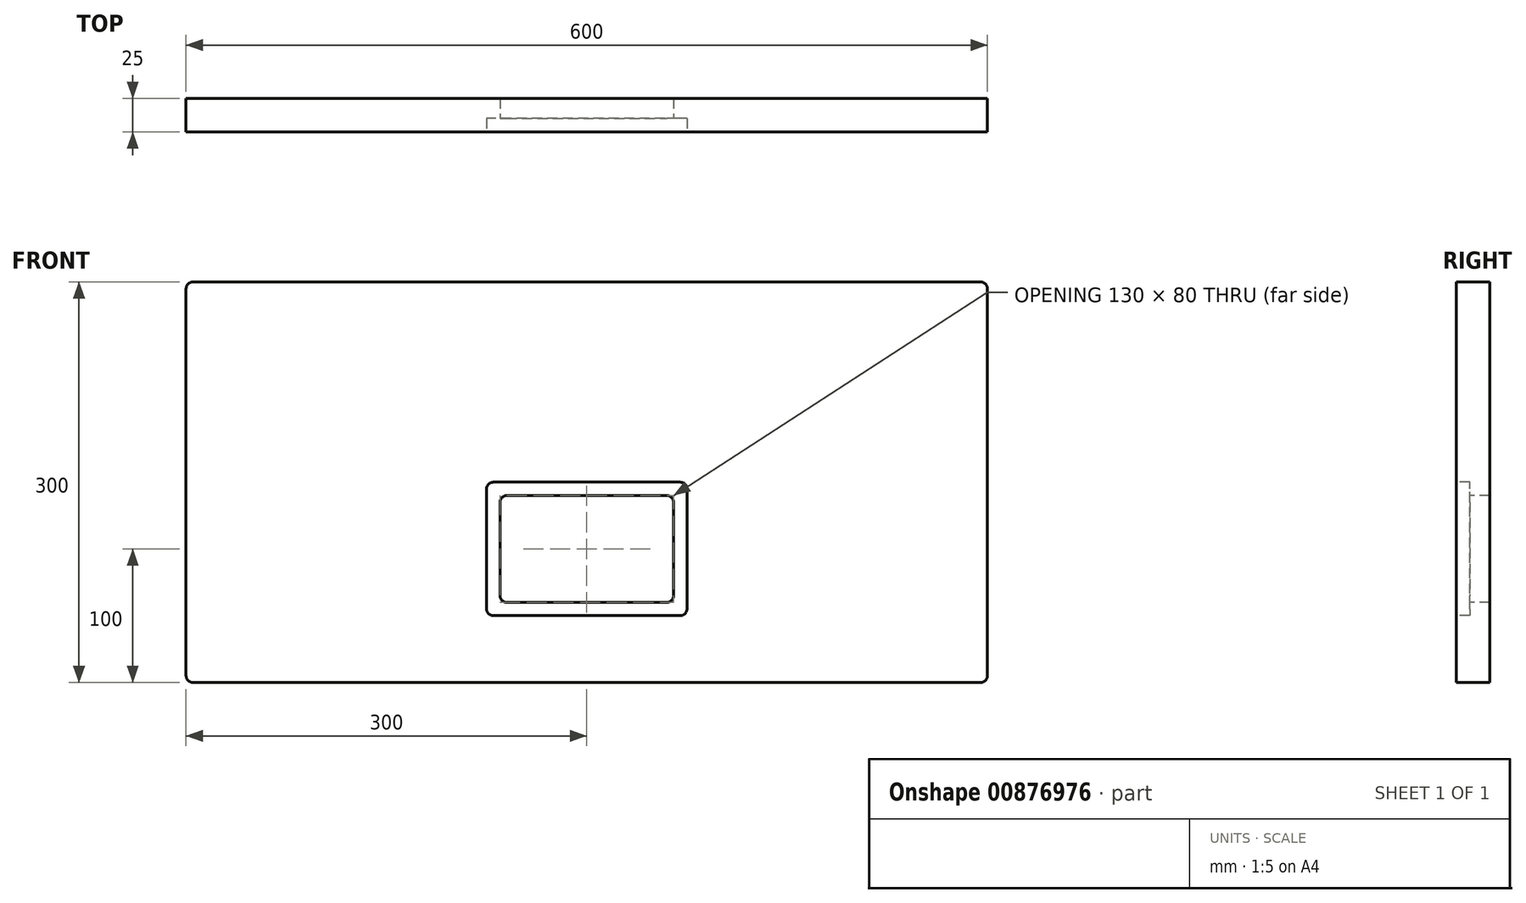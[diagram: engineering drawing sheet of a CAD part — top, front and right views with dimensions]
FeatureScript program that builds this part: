
annotation { "Feature Type Name" : "Feature", "Feature Type Description" : "" }
export const myFeature = defineFeature(function(context is Context, id is Id, definition is map)
    precondition{}
    {
        {
            var Q0;
            Q0=qCreatedBy(makeId("Front.planeOp"),FACE);
            var sketch = newSketch(context, id + "F0", { "sketchPlane" : qUnion([Q0])});
            skLineSegment(sketch, "E0.bottom", {"start": v(300, -150) * mm, "end": v(-300, -150) * mm});
            skLineSegment(sketch, "E0.top", {"start": v(300, 150) * mm, "end": v(-300, 150) * mm});
            skLineSegment(sketch, "E0.left", {"start": v(300, -150) * mm, "end": v(300, 150) * mm});
            skLineSegment(sketch, "E0.right", {"start": v(-300, -150) * mm, "end": v(-300, 150) * mm});
            skPoint(sketch, "E0.middle", {"position": v(0, 0) * mm});
            skSolve(sketch);
        }
        {
            var Q0;
            Q0 = qSketchRegion(id + "F0", true);
            extrude(context, id + "F1", {"entities" : qUnion([Q0]), "oppositeDirection" : true, "depth" : 25 * mm, "offsetDistance" : 25 * mm});
        }
        {
            var Q0;
            Q0=makeQuery(id+"F1.opExtrude","SWEPT_EDGE",EDGE,{"disambiguationData":[OSD([sQuery(id+"F0.wireOp",EDGE,"E0.bottom"),sQuery(id+"F0.wireOp",EDGE,"E0.left")])]});
            var Q1;
            Q1=makeQuery(id+"F1.opExtrude","SWEPT_EDGE",EDGE,{"disambiguationData":[OSD([sQuery(id+"F0.wireOp",EDGE,"E0.bottom"),sQuery(id+"F0.wireOp",EDGE,"E0.right")])]});
            var Q2;
            Q2=makeQuery(id+"F1.opExtrude","SWEPT_EDGE",EDGE,{"disambiguationData":[OSD([sQuery(id+"F0.wireOp",EDGE,"E0.top"),sQuery(id+"F0.wireOp",EDGE,"E0.left")])]});
            var Q3;
            Q3=makeQuery(id+"F1.opExtrude","SWEPT_EDGE",EDGE,{"disambiguationData":[OSD([sQuery(id+"F0.wireOp",EDGE,"E0.top"),sQuery(id+"F0.wireOp",EDGE,"E0.right")])]});
            fillet(context, id + "F2", {"entities" : qUnion([Q0, Q1, Q2, Q3]), "radius" : 5 * mm, "tangentPropagation" : true, "allowEdgeOverflow" : false});
        }
        {
            var Q0;
            Q0=makeQuery(id+"F1.opExtrude","CAP_FACE",FACE,{"disambiguationData":[OSD([sQuery(id+"F0.wireOp",EDGE,"E0.bottom"),sQuery(id+"F0.wireOp",EDGE,"E0.top"),sQuery(id+"F0.wireOp",EDGE,"E0.left"),sQuery(id+"F0.wireOp",EDGE,"E0.right")])],"isStart":true});
            var sketch = newSketch(context, id + "F3", { "sketchPlane" : qUnion([Q0])});
            skLineSegment(sketch, "E1.bottom", {"start": v(70, -100) * mm, "end": v(-70, -100) * mm});
            skLineSegment(sketch, "E1.top", {"start": v(70, 0) * mm, "end": v(-70, 0) * mm});
            skLineSegment(sketch, "E1.left", {"start": v(75, -95) * mm, "end": v(75, -5) * mm});
            skLineSegment(sketch, "E1.right", {"start": v(-75, -95) * mm, "end": v(-75, -5) * mm});
            skPoint(sketch, "E1.middle", {"position": v(0, -50) * mm});
            skPoint(sketch, "E2.visualSharp", {"position": v(-75, 0) * mm});
            skArc(sketch, "E2.filletArc", {"start": v(-70, 0) * mm, "mid": v(-73.54, -1.46) * mm, "end": v(-75, -5) * mm});
            skPoint(sketch, "E3.visualSharp", {"position": v(75, 0) * mm});
            skArc(sketch, "E3.filletArc", {"start": v(75, -5) * mm, "mid": v(73.54, -1.46) * mm, "end": v(70, 0) * mm});
            skPoint(sketch, "E4.visualSharp", {"position": v(75, -100) * mm});
            skArc(sketch, "E4.filletArc", {"start": v(70, -100) * mm, "mid": v(73.54, -98.54) * mm, "end": v(75, -95) * mm});
            skPoint(sketch, "E5.visualSharp", {"position": v(-75, -100) * mm});
            skArc(sketch, "E5.filletArc", {"start": v(-75, -95) * mm, "mid": v(-73.54, -98.54) * mm, "end": v(-70, -100) * mm});
            skSolve(sketch);
        }
        {
            var Q0;
            Q0 = qSketchRegion(id + "F3", true);
            extrude(context, id + "F4", {"entities" : qUnion([Q0]), "operationType" : NewBodyOperationType.REMOVE, "oppositeDirection" : true, "depth" : 10 * mm, "offsetDistance" : 25 * mm});
        }
        {
            var Q0;
            Q0=makeQuery(id+"F4.boolean.opBoolean","COPY",FACE,{"derivedFrom":makeQuery(id+"F4.opExtrude","CAP_FACE",FACE,{"disambiguationData":[OSD([sQuery(id+"F3.wireOp",EDGE,"E1.bottom"),sQuery(id+"F3.wireOp",EDGE,"E1.top"),sQuery(id+"F3.wireOp",EDGE,"E1.left"),sQuery(id+"F3.wireOp",EDGE,"E1.right")])],"isStart":false})});
            var sketch = newSketch(context, id + "F5", { "sketchPlane" : qUnion([Q0])});
            skLineSegment(sketch, "E6.bottom", {"start": v(-60, -10) * mm, "end": v(60, -10) * mm});
            skLineSegment(sketch, "E6.top", {"start": v(-60, -90) * mm, "end": v(60, -90) * mm});
            skLineSegment(sketch, "E6.left", {"start": v(-65, -15) * mm, "end": v(-65, -85) * mm});
            skLineSegment(sketch, "E6.right", {"start": v(65, -15) * mm, "end": v(65, -85) * mm});
            skPoint(sketch, "E7.visualSharp", {"position": v(65, -10) * mm});
            skArc(sketch, "E7.filletArc", {"start": v(65, -15) * mm, "mid": v(63.54, -11.46) * mm, "end": v(60, -10) * mm});
            skPoint(sketch, "E8.visualSharp", {"position": v(-65, -10) * mm});
            skArc(sketch, "E8.filletArc", {"start": v(-60, -10) * mm, "mid": v(-63.54, -11.46) * mm, "end": v(-65, -15) * mm});
            skPoint(sketch, "E9.visualSharp", {"position": v(65, -90) * mm});
            skArc(sketch, "E9.filletArc", {"start": v(60, -90) * mm, "mid": v(63.54, -88.54) * mm, "end": v(65, -85) * mm});
            skPoint(sketch, "E10.visualSharp", {"position": v(-65, -90) * mm});
            skArc(sketch, "E10.filletArc", {"start": v(-65, -85) * mm, "mid": v(-63.54, -88.54) * mm, "end": v(-60, -90) * mm});
            skSolve(sketch);
        }
        {
            var Q0;
            Q0 = qSketchRegion(id + "F5", true);
            extrude(context, id + "F6", {"entities" : qUnion([Q0]), "operationType" : NewBodyOperationType.REMOVE, "oppositeDirection" : true, "depth" : 25 * mm, "offsetDistance" : 25 * mm});
        }
    });
